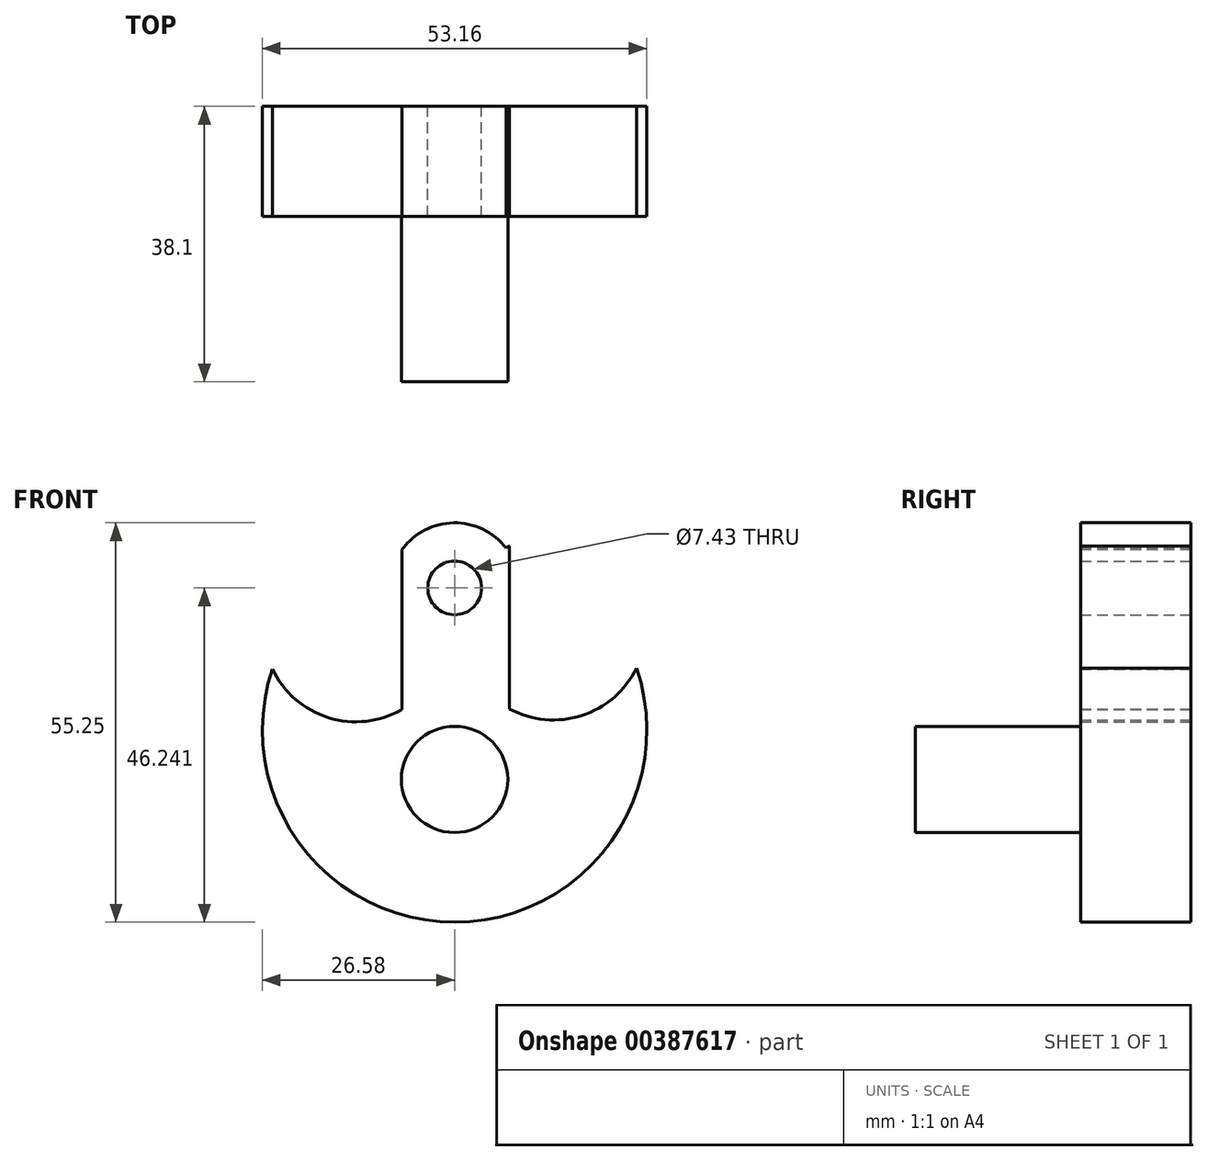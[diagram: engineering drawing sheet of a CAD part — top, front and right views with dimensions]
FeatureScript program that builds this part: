
annotation { "Feature Type Name" : "Feature", "Feature Type Description" : "" }
export const myFeature = defineFeature(function(context is Context, id is Id, definition is map)
    precondition{}
    {
        {
            var Q0;
            Q0=qCreatedBy(makeId("Front.planeOp"),FACE);
            var sketch = newSketch(context, id + "F0", { "sketchPlane" : qUnion([Q0])});
            skArc(sketch, "E0", {"start": v(-25.2, 8.44) * mm, "mid": v(0.07, -26.58) * mm, "end": v(25.15, 8.58) * mm});
            skArc(sketch, "E1", {"start": v(7.59, 25.47) * mm, "mid": v(7.35, 25.34) * mm, "end": v(7.1, 25.2) * mm});
            skArc(sketch, "E2", {"start": v(-25.2, 8.44) * mm, "mid": v(-17.45, 1.72) * mm, "end": v(-7.26, 2.86) * mm});
            skArc(sketch, "E3", {"start": v(7.59, 24.51) * mm, "mid": v(0.3, 28.66) * mm, "end": v(-7.26, 25) * mm});
            skArc(sketch, "E4.trimOffspring", {"start": v(7.59, 2.93) * mm, "mid": v(17.58, 2.02) * mm, "end": v(25.15, 8.58) * mm});
            skArc(sketch, "E5.trimOffspring", {"start": v(-7.26, 25) * mm, "mid": v(-7.6, 25.19) * mm, "end": v(-7.94, 25.36) * mm});
            skLineSegment(sketch, "E6", {"start": v(-7.26, 25) * mm, "end": v(-7.26, 2.86) * mm});
            skLineSegment(sketch, "E7", {"start": v(7.59, 25.47) * mm, "end": v(7.59, 2.93) * mm});
            skCircle(sketch, "E8", {"center": v(0, 19.66) * mm, "radius": 3.71 * mm});
            skCircle(sketch, "E9", {"center": v(0, -6.83) * mm, "radius": 7.35 * mm});
            skSolve(sketch);
        }
        {
            var Q0;
            Q0 = qSketchRegion(id + "F0", true);
            extrude(context, id + "F1", {"entities" : qUnion([Q0]), "depth" : 15.24 * mm});
        }
        {
            var Q0;
            Q0=makeQuery(id+"F0.imprint","IMPRINT",FACE,{"disambiguationData":[TD([[makeQuery(id+"F0.imprint","IMPRINT",EDGE,{"derivedFrom":sQuery(id+"F0.wireOp",EDGE,"E9")}),1.0]])]});
            extrude(context, id + "F2", {"entities" : qUnion([Q0]), "operationType" : NewBodyOperationType.ADD, "depth" : 38.1 * mm});
        }
    });
